AUTODESK INVENTOR PART (.ipt)
format: ipt  version: 2021.3 (Build 253353000, 353)  size: 281,600 bytes
history: native  units: mm
features: other x4, sketch x3, extrude x1, plane x1
ambient origin geometry x8: Origin, YZ Plane, XZ Plane, XY Plane, X Axis, Y Axis, Z Axis, Center Point
bodies: Body (feature_tree)
feature tree (9):
  other  "Driven Length"
  other  "Frame Generator"
  extrude  "Extrusion_20x20"  Depth=1.5mm
  other  "Start Plane"
  other  "End Plane"
  sketch  "Sketch"  dims[d7=3.0mm d9=1.5mm d10=0.5mm d13=0.5mm d14=0.5mm d18=3.0mm d19=3.0mm d21=0.5mm d22=0.5mm d23=0.5mm d24=2.75mm d25=1.5mm d26=10.0mm d27=10.0mm d28=3.0mm d29=3.0mm d30=5.5mm d31=1.5mm d32=0.5mm d33=0.5mm d34=0.5mm d35=0.5mm d36=0.5mm d37=0.5mm d38=0.5mm d39=0.5mm d40=0.5mm d41=2.75mm d42=2.75mm d43=0.5mm d44=40.0mm d46=360.0deg d50=-0.0mm d51=660.0mm d52=0.13mm d53=0.0mm d54=90.0deg d55=660.0mm]
  sketch  "Sketch2"  dims[d4=5.5mm d5=1.5mm]
  plane  "Work Plane3"
  sketch  "Sketch3"  dims[d6=1.5mm]
